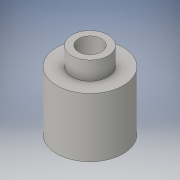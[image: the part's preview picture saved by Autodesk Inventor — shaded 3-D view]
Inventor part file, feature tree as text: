
AUTODESK INVENTOR PART (.ipt)
format: ipt  version: 2016 (Build 200138000, 138)  size: 105,984 bytes
history: native  units: in
note: dims shown in document units (in); Inventor stores cm internally (conversion verified against a paired STEP export)
features: extrude x3, sketch x3
ambient origin geometry x8: Origin, YZ Plane, XZ Plane, XY Plane, X Axis, Y Axis, Z Axis, Center Point
bodies: Solid1 (feature_tree)
feature tree (6):
  extrude  "Extrusion1"  Depth=0.83in TaperAngle=0.0deg
  extrude  "Extrusion2"  Depth=0.711in
  extrude  "Extrusion3"  Depth=0.196in
  sketch  "Sketch1"  dims[d0=0.711in d1=0.83in d2=0.0in]
  sketch  "Sketch2"  dims[d3=0.388in d4=0.711in]
  sketch  "Sketch3"  dims[d5=0.196in d6=0.0in d7=0.2465in d8=8.0in d9=0.0in]
